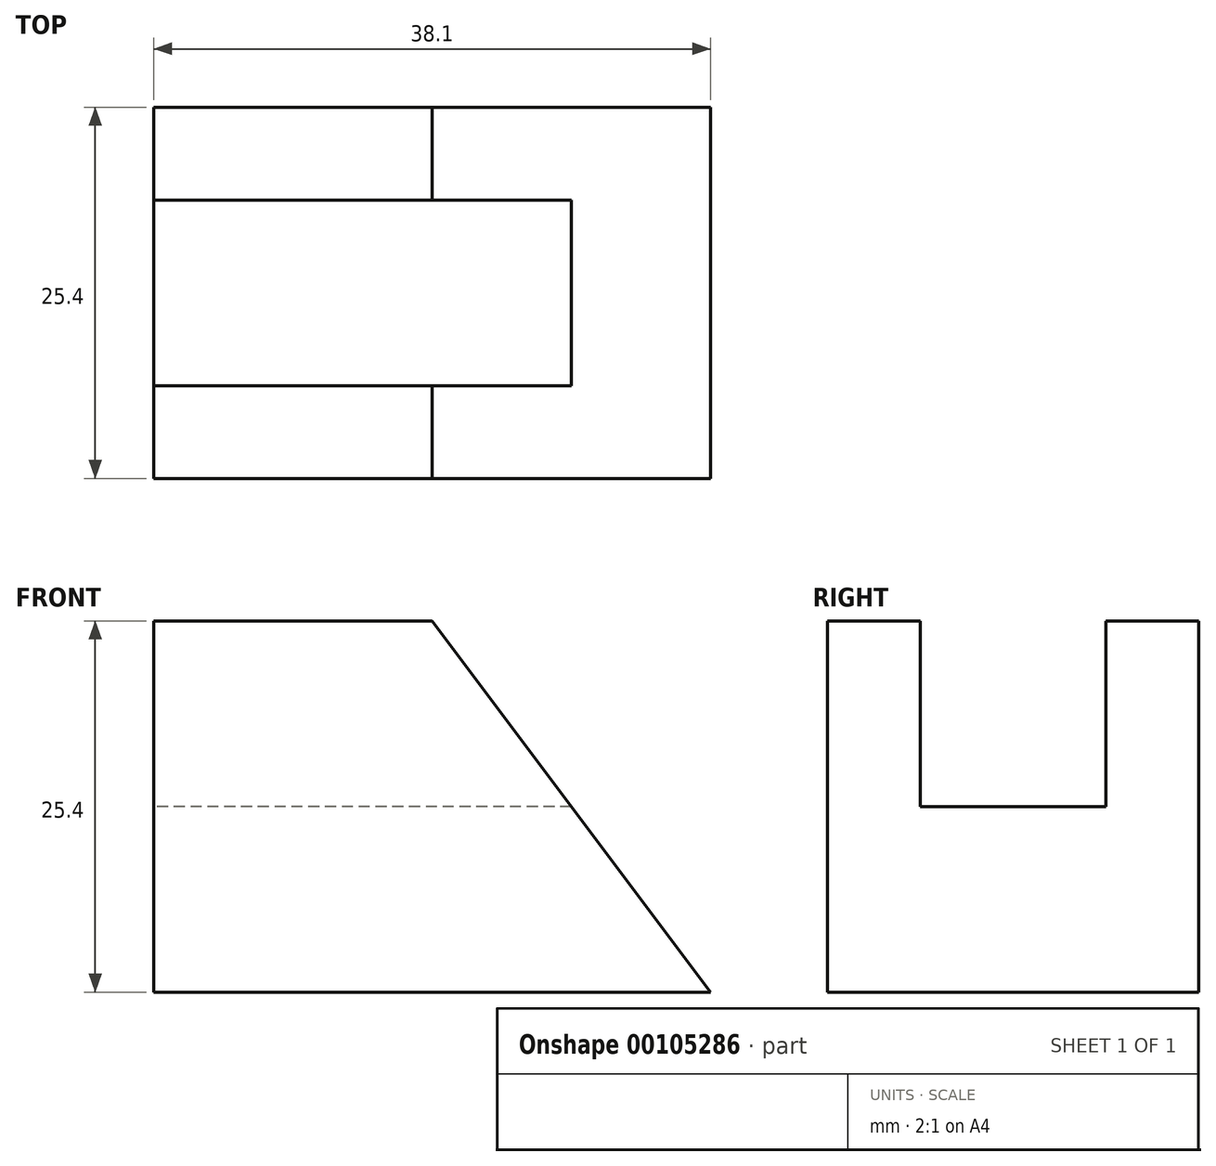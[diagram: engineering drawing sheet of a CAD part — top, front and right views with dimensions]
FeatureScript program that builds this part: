
annotation { "Feature Type Name" : "Feature", "Feature Type Description" : "" }
export const myFeature = defineFeature(function(context is Context, id is Id, definition is map)
    precondition{}
    {
        {
            var Q0;
            Q0=qCreatedBy(makeId("Front.planeOp"),FACE);
            var sketch = newSketch(context, id + "F0", { "sketchPlane" : qUnion([Q0])});
            skLineSegment(sketch, "E0", {"start": v(0, 0) * mm, "end": v(38.1, 0) * mm});
            skLineSegment(sketch, "E1", {"start": v(38.1, 0) * mm, "end": v(19.05, 25.4) * mm});
            skLineSegment(sketch, "E2", {"start": v(19.05, 25.4) * mm, "end": v(0, 25.4) * mm});
            skLineSegment(sketch, "E3", {"start": v(0, 25.4) * mm, "end": v(0, 0) * mm});
            skLineSegment(sketch, "E4", {"start": v(0, 12.7) * mm, "end": v(28.58, 12.7) * mm});
            skSolve(sketch);
        }
        {
            var Q0;
            {var subQ0=sQuery(id+"F0.wireOp",EDGE,"E0");Q0=makeQuery(id+"F0.imprint","IMPRINT",FACE,{"disambiguationData":[TD([[makeQuery(id+"F0.imprint","IMPRINT",EDGE,{"derivedFrom":subQ0}),1.0]])]});}
            extrude(context, id + "F1", {"entities" : qUnion([Q0]), "oppositeDirection" : true, "depth" : 25.4 * mm});
        }
        {
            var Q0;
            {var subQ0=sQuery(id+"F0.wireOp",EDGE,"E2");Q0=makeQuery(id+"F0.imprint","IMPRINT",FACE,{"disambiguationData":[TD([[makeQuery(id+"F0.imprint","IMPRINT",EDGE,{"derivedFrom":subQ0}),1.0]])]});}
            extrude(context, id + "F2", {"entities" : qUnion([Q0]), "operationType" : NewBodyOperationType.ADD, "oppositeDirection" : true, "depth" : 25.4 * mm});
        }
        {
            var Q0;
            Q0=makeQuery(id+"F2.opExtrude","SWEPT_FACE",FACE,{"disambiguationData":[OSD([sQuery(id+"F0.wireOp",EDGE,"E2")])]});
            var sketch = newSketch(context, id + "F3", { "sketchPlane" : qUnion([Q0])});
            skLineSegment(sketch, "E5.bottom", {"start": v(19.05, 6.35) * mm, "end": v(0, 6.35) * mm});
            skLineSegment(sketch, "E5.top", {"start": v(19.05, 19.05) * mm, "end": v(0, 19.05) * mm});
            skLineSegment(sketch, "E5.left", {"start": v(19.05, 6.35) * mm, "end": v(19.05, 19.05) * mm});
            skLineSegment(sketch, "E5.right", {"start": v(0, 6.35) * mm, "end": v(0, 19.05) * mm});
            skPoint(sketch, "E5.middle", {"position": v(9.53, 12.7) * mm});
            skPoint(sketch, "E5.middle.positionSnap0", {"position": v(9.53, 0) * mm});
            skPoint(sketch, "E5.middle.positionSnap1", {"position": v(0, 12.7) * mm});
            skPoint(sketch, "E5.centerSnap0", {"position": v(9.53, 0) * mm});
            skPoint(sketch, "E5.centerSnap1", {"position": v(0, 12.7) * mm});
            skSolve(sketch);
        }
        {
            var Q0;
            Q0=makeQuery(id+"F3.imprint","IMPRINT",FACE,{"disambiguationData":[TD([[makeQuery(id+"F3.imprint","IMPRINT",EDGE,{"derivedFrom":sQuery(id+"F3.wireOp",EDGE,"E5.bottom")}),-1.0]])]});
            extrude(context, id + "F4", {"entities" : qUnion([Q0]), "operationType" : NewBodyOperationType.REMOVE, "oppositeDirection" : true, "depth" : 12.7 * mm});
        }
        {
            var Q0;
            Q0=makeQuery(id+"F4.boolean.opBoolean","COPY",FACE,{"derivedFrom":makeQuery(id+"F4.opExtrude","SWEPT_FACE",FACE,{"disambiguationData":[OSD([sQuery(id+"F3.wireOp",EDGE,"E5.left")])]})});
            extrude(context, id + "F5", {"entities" : qUnion([Q0]), "operationType" : NewBodyOperationType.REMOVE, "oppositeDirection" : true, "depth" : 25.4 * mm});
        }
    });
